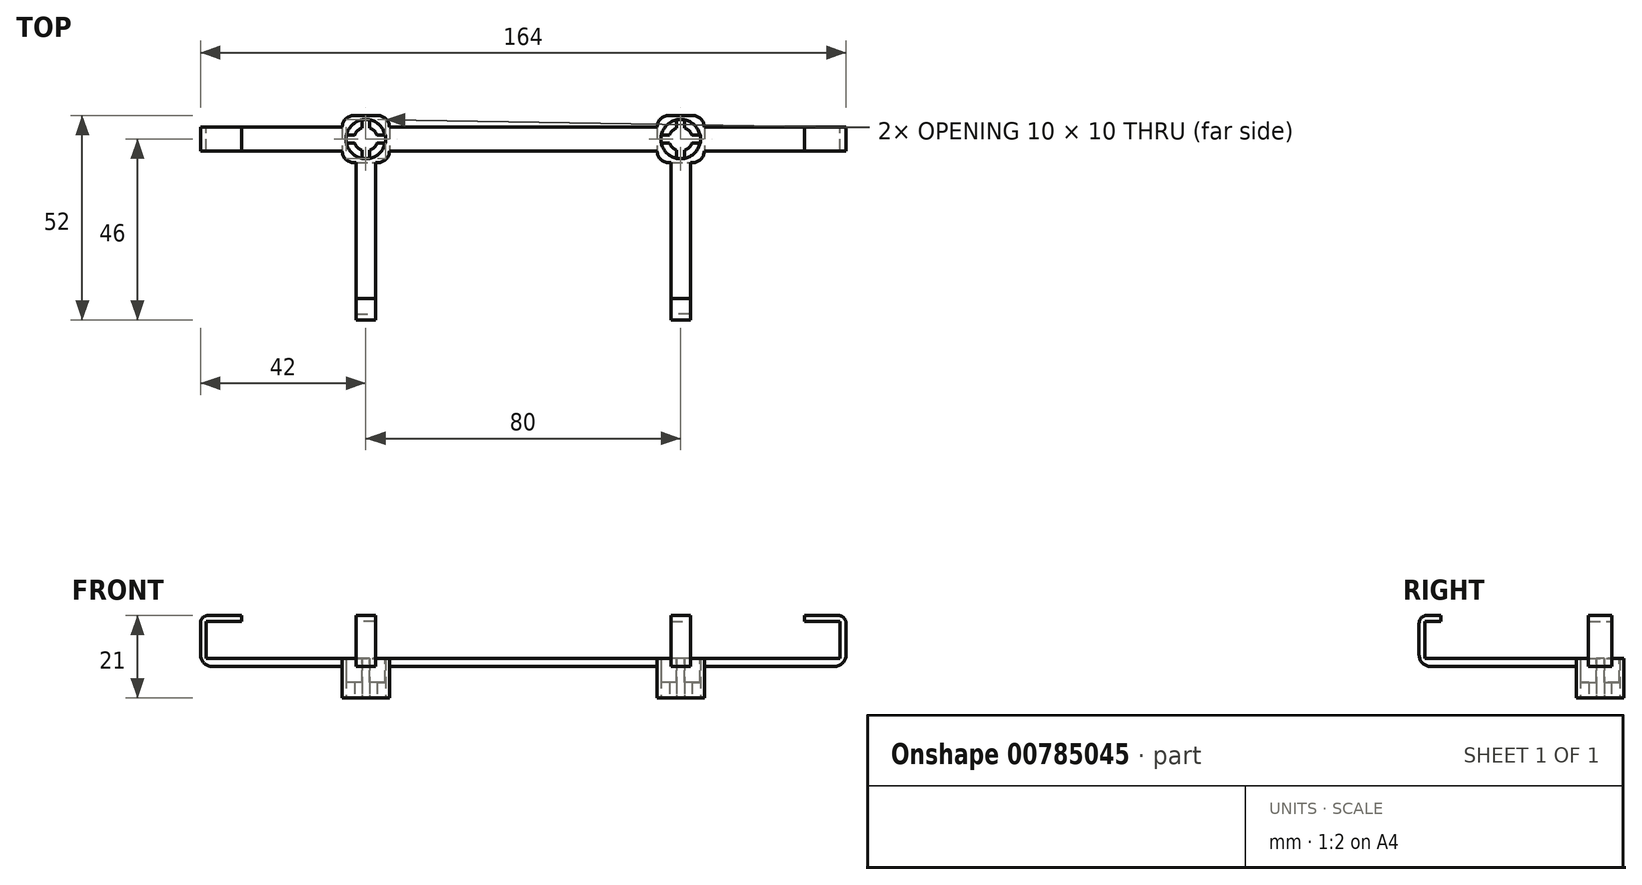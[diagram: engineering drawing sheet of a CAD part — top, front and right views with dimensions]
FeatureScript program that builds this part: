
annotation { "Feature Type Name" : "Feature", "Feature Type Description" : "" }
export const myFeature = defineFeature(function(context is Context, id is Id, definition is map)
    precondition{}
    {
        {
            var Q0;
            Q0=qCreatedBy(makeId("Top.planeOp"),FACE);
            var sketch = newSketch(context, id + "F0", { "sketchPlane" : qUnion([Q0])});
            skLineSegment(sketch, "E0.bottom", {"start": v(82, 3) * mm, "end": v(-82, 3) * mm});
            skLineSegment(sketch, "E0.top", {"start": v(82, -3) * mm, "end": v(-82, -3) * mm});
            skLineSegment(sketch, "E0.left", {"start": v(82, 3) * mm, "end": v(82, -3) * mm});
            skLineSegment(sketch, "E0.right", {"start": v(-82, 3) * mm, "end": v(-82, -3) * mm});
            skPoint(sketch, "E0.middle", {"position": v(0, 0) * mm});
            skLineSegment(sketch, "E1", {"start": v(0, 0) * mm, "end": v(-40, 0) * mm});
            skLineSegment(sketch, "E2", {"start": v(0, 0) * mm, "end": v(40, 0) * mm});
            skLineSegment(sketch, "E3.bottom", {"start": v(-46, 6) * mm, "end": v(-34, 6) * mm});
            skLineSegment(sketch, "E3.top", {"start": v(-46, -6) * mm, "end": v(-34, -6) * mm});
            skLineSegment(sketch, "E3.left", {"start": v(-46, 6) * mm, "end": v(-46, -6) * mm});
            skLineSegment(sketch, "E3.right", {"start": v(-34, 6) * mm, "end": v(-34, -6) * mm});
            skPoint(sketch, "E3.middle", {"position": v(-40, 0) * mm});
            skPoint(sketch, "E4.MirrorP", {"position": v(40, 0) * mm});
            skLineSegment(sketch, "E5.MirrorCS", {"start": v(34, 6) * mm, "end": v(34, -6) * mm});
            skLineSegment(sketch, "E6.MirrorCS", {"start": v(46, 6) * mm, "end": v(46, -6) * mm});
            skLineSegment(sketch, "E7.MirrorCS", {"start": v(46, 6) * mm, "end": v(34, 6) * mm});
            skLineSegment(sketch, "E8.MirrorCS", {"start": v(46, -6) * mm, "end": v(34, -6) * mm});
            skLineSegment(sketch, "E9", {"start": v(-40, -6) * mm, "end": v(-40, -46) * mm});
            skLineSegment(sketch, "E10", {"start": v(-40, -46) * mm, "end": v(-37.5, -46) * mm});
            skLineSegment(sketch, "E11", {"start": v(-37.5, -46) * mm, "end": v(-37.5, -6) * mm});
            skLineSegment(sketch, "E12", {"start": v(-40, -46) * mm, "end": v(-42.5, -46) * mm});
            skLineSegment(sketch, "E13", {"start": v(-42.5, -46) * mm, "end": v(-42.5, -6) * mm});
            skLineSegment(sketch, "E14", {"start": v(0, 0) * mm, "end": v(0, -52.19) * mm});
            skPoint(sketch, "E14.endSnap0", {"position": v(0, -3) * mm});
            skLineSegment(sketch, "E15.MirrorCS", {"start": v(40, -46) * mm, "end": v(42.5, -46) * mm});
            skLineSegment(sketch, "E16.MirrorCS", {"start": v(37.5, -46) * mm, "end": v(37.5, -6) * mm});
            skLineSegment(sketch, "E17.MirrorCS", {"start": v(42.5, -46) * mm, "end": v(42.5, -6) * mm});
            skLineSegment(sketch, "E18.MirrorCS", {"start": v(40, -46) * mm, "end": v(37.5, -46) * mm});
            skLineSegment(sketch, "E19.MirrorCS", {"start": v(40, -6) * mm, "end": v(40, -46) * mm});
            skSolve(sketch);
        }
        {
            var Q0;
            Q0 = qSketchRegion(id + "F0", true);
            extrude(context, id + "F1", {"entities" : qUnion([Q0]), "depth" : 2 * mm, "offsetDistance" : 25 * mm});
        }
        {
            var Q0;
            Q0=makeQuery(id+"F1.opExtrude","CAP_FACE",FACE,{"disambiguationData":[OSD([sQuery(id+"F0.wireOp",EDGE,"E0.bottom"),sQuery(id+"F0.wireOp",EDGE,"E0.top"),sQuery(id+"F0.wireOp",EDGE,"E0.left"),sQuery(id+"F0.wireOp",EDGE,"E0.right"),sQuery(id+"F0.wireOp",EDGE,"E3.bottom"),sQuery(id+"F0.wireOp",EDGE,"E3.top"),sQuery(id+"F0.wireOp",EDGE,"E3.left"),sQuery(id+"F0.wireOp",EDGE,"E3.right"),sQuery(id+"F0.wireOp",EDGE,"E5.MirrorCS"),sQuery(id+"F0.wireOp",EDGE,"E6.MirrorCS"),sQuery(id+"F0.wireOp",EDGE,"E7.MirrorCS"),sQuery(id+"F0.wireOp",EDGE,"E8.MirrorCS"),sQuery(id+"F0.wireOp",EDGE,"E10"),sQuery(id+"F0.wireOp",EDGE,"E11"),sQuery(id+"F0.wireOp",EDGE,"E12"),sQuery(id+"F0.wireOp",EDGE,"E13"),sQuery(id+"F0.wireOp",EDGE,"E15.MirrorCS"),sQuery(id+"F0.wireOp",EDGE,"E16.MirrorCS"),sQuery(id+"F0.wireOp",EDGE,"E17.MirrorCS"),sQuery(id+"F0.wireOp",EDGE,"E18.MirrorCS")])],"isStart":false});
            var sketch = newSketch(context, id + "F2", { "sketchPlane" : qUnion([Q0])});
            skLineSegment(sketch, "E20.bottom", {"start": v(-42.5, -46) * mm, "end": v(-37.5, -46) * mm});
            skLineSegment(sketch, "E20.top", {"start": v(-42.5, -44.5) * mm, "end": v(-37.5, -44.5) * mm});
            skLineSegment(sketch, "E20.left", {"start": v(-42.5, -46) * mm, "end": v(-42.5, -44.5) * mm});
            skLineSegment(sketch, "E20.right", {"start": v(-37.5, -46) * mm, "end": v(-37.5, -44.5) * mm});
            skLineSegment(sketch, "E21.MirrorCS", {"start": v(42.5, -46) * mm, "end": v(42.5, -44.5) * mm});
            skLineSegment(sketch, "E22.MirrorCS", {"start": v(37.5, -46) * mm, "end": v(37.5, -44.5) * mm});
            skLineSegment(sketch, "E23.MirrorCS", {"start": v(42.5, -44.5) * mm, "end": v(37.5, -44.5) * mm});
            skLineSegment(sketch, "E24.MirrorCS", {"start": v(42.5, -46) * mm, "end": v(37.5, -46) * mm});
            skLineSegment(sketch, "E25.bottom", {"start": v(-82, -3) * mm, "end": v(-80.5, -3) * mm});
            skLineSegment(sketch, "E25.top", {"start": v(-82, 3) * mm, "end": v(-80.5, 3) * mm});
            skLineSegment(sketch, "E25.left", {"start": v(-82, -3) * mm, "end": v(-82, 3) * mm});
            skLineSegment(sketch, "E25.right", {"start": v(-80.5, -3) * mm, "end": v(-80.5, 3) * mm});
            skLineSegment(sketch, "E26.MirrorCS", {"start": v(82, -3) * mm, "end": v(80.5, -3) * mm});
            skLineSegment(sketch, "E27.MirrorCS", {"start": v(82, 3) * mm, "end": v(80.5, 3) * mm});
            skLineSegment(sketch, "E28.MirrorCS", {"start": v(80.5, -3) * mm, "end": v(80.5, 3) * mm});
            skLineSegment(sketch, "E29.MirrorCS", {"start": v(82, -3) * mm, "end": v(82, 3) * mm});
            skSolve(sketch);
        }
        {
            var Q0;
            Q0 = qSketchRegion(id + "F2", true);
            extrude(context, id + "F3", {"entities" : qUnion([Q0]), "operationType" : NewBodyOperationType.ADD, "depth" : 11 * mm, "offsetDistance" : 25 * mm});
        }
        {
            var Q0;
            Q0=makeQuery(id+"F3.opExtrude","SWEPT_FACE",FACE,{"disambiguationData":[OSD([sQuery(id+"F2.wireOp",EDGE,"E20.top")])]});
            var sketch = newSketch(context, id + "F4", { "sketchPlane" : qUnion([Q0])});
            skLineSegment(sketch, "E30.bottom", {"start": v(37.5, 13) * mm, "end": v(42.5, 13) * mm});
            skLineSegment(sketch, "E30.top", {"start": v(37.5, 11.5) * mm, "end": v(42.5, 11.5) * mm});
            skLineSegment(sketch, "E30.left", {"start": v(37.5, 13) * mm, "end": v(37.5, 11.5) * mm});
            skLineSegment(sketch, "E30.right", {"start": v(42.5, 13) * mm, "end": v(42.5, 11.5) * mm});
            skLineSegment(sketch, "E31", {"start": v(0, 7.91) * mm, "end": v(0, 17.58) * mm});
            skLineSegment(sketch, "E32.MirrorCS", {"start": v(-37.5, 13) * mm, "end": v(-37.5, 11.5) * mm});
            skLineSegment(sketch, "E33.MirrorCS", {"start": v(-42.5, 13) * mm, "end": v(-42.5, 11.5) * mm});
            skLineSegment(sketch, "E34.MirrorCS", {"start": v(-37.5, 11.5) * mm, "end": v(-42.5, 11.5) * mm});
            skLineSegment(sketch, "E35.MirrorCS", {"start": v(-37.5, 13) * mm, "end": v(-42.5, 13) * mm});
            skSolve(sketch);
        }
        {
            var Q0;
            Q0 = qSketchRegion(id + "F4", true);
            extrude(context, id + "F5", {"entities" : qUnion([Q0]), "operationType" : NewBodyOperationType.ADD, "depth" : 4 * mm, "offsetDistance" : 25 * mm});
        }
        {
            var Q0;
            Q0=makeQuery(id+"F3.opExtrude","SWEPT_FACE",FACE,{"disambiguationData":[OSD([sQuery(id+"F2.wireOp",EDGE,"E28.MirrorCS")])]});
            var sketch = newSketch(context, id + "F6", { "sketchPlane" : qUnion([Q0])});
            skLineSegment(sketch, "E36.bottom", {"start": v(-3, 13) * mm, "end": v(3, 13) * mm});
            skLineSegment(sketch, "E36.top", {"start": v(-3, 11.5) * mm, "end": v(3, 11.5) * mm});
            skLineSegment(sketch, "E36.left", {"start": v(-3, 13) * mm, "end": v(-3, 11.5) * mm});
            skLineSegment(sketch, "E36.right", {"start": v(3, 13) * mm, "end": v(3, 11.5) * mm});
            skSolve(sketch);
        }
        {
            var Q0;
            Q0 = qSketchRegion(id + "F6", true);
            extrude(context, id + "F7", {"entities" : qUnion([Q0]), "operationType" : NewBodyOperationType.ADD, "depth" : 9 * mm, "offsetDistance" : 25 * mm});
        }
        {
            var Q0;
            Q0=makeQuery(id+"F3.opExtrude","SWEPT_FACE",FACE,{"disambiguationData":[OSD([sQuery(id+"F2.wireOp",EDGE,"E25.right")])]});
            var sketch = newSketch(context, id + "F8", { "sketchPlane" : qUnion([Q0])});
            skLineSegment(sketch, "E37.bottom", {"start": v(-3, 13) * mm, "end": v(3, 13) * mm});
            skLineSegment(sketch, "E37.top", {"start": v(-3, 11.5) * mm, "end": v(3, 11.5) * mm});
            skLineSegment(sketch, "E37.left", {"start": v(-3, 13) * mm, "end": v(-3, 11.5) * mm});
            skLineSegment(sketch, "E37.right", {"start": v(3, 13) * mm, "end": v(3, 11.5) * mm});
            skSolve(sketch);
        }
        {
            var Q0;
            Q0 = qSketchRegion(id + "F8", true);
            extrude(context, id + "F9", {"entities" : qUnion([Q0]), "operationType" : NewBodyOperationType.ADD, "depth" : 9 * mm, "offsetDistance" : 25 * mm});
        }
        {
            var Q0;
            Q0=makeQuery(id+"F1.opExtrude","CAP_FACE",FACE,{"disambiguationData":[OSD([sQuery(id+"F0.wireOp",EDGE,"E0.bottom"),sQuery(id+"F0.wireOp",EDGE,"E0.top"),sQuery(id+"F0.wireOp",EDGE,"E0.left"),sQuery(id+"F0.wireOp",EDGE,"E0.right"),sQuery(id+"F0.wireOp",EDGE,"E3.bottom"),sQuery(id+"F0.wireOp",EDGE,"E3.top"),sQuery(id+"F0.wireOp",EDGE,"E3.left"),sQuery(id+"F0.wireOp",EDGE,"E3.right"),sQuery(id+"F0.wireOp",EDGE,"E5.MirrorCS"),sQuery(id+"F0.wireOp",EDGE,"E6.MirrorCS"),sQuery(id+"F0.wireOp",EDGE,"E7.MirrorCS"),sQuery(id+"F0.wireOp",EDGE,"E8.MirrorCS"),sQuery(id+"F0.wireOp",EDGE,"E10"),sQuery(id+"F0.wireOp",EDGE,"E11"),sQuery(id+"F0.wireOp",EDGE,"E12"),sQuery(id+"F0.wireOp",EDGE,"E13"),sQuery(id+"F0.wireOp",EDGE,"E15.MirrorCS"),sQuery(id+"F0.wireOp",EDGE,"E16.MirrorCS"),sQuery(id+"F0.wireOp",EDGE,"E17.MirrorCS"),sQuery(id+"F0.wireOp",EDGE,"E18.MirrorCS")])],"isStart":true});
            var sketch = newSketch(context, id + "F10", { "sketchPlane" : qUnion([Q0])});
            skLineSegment(sketch, "E38.bottom", {"start": v(-46, 6) * mm, "end": v(-34, 6) * mm});
            skLineSegment(sketch, "E38.top", {"start": v(-46, -6) * mm, "end": v(-34, -6) * mm});
            skLineSegment(sketch, "E38.left", {"start": v(-46, 6) * mm, "end": v(-46, -6) * mm});
            skLineSegment(sketch, "E38.right", {"start": v(-34, 6) * mm, "end": v(-34, -6) * mm});
            skLineSegment(sketch, "E39.bottom", {"start": v(34, 6) * mm, "end": v(46, 6) * mm});
            skLineSegment(sketch, "E39.top", {"start": v(34, -6) * mm, "end": v(46, -6) * mm});
            skLineSegment(sketch, "E39.left", {"start": v(34, 6) * mm, "end": v(34, -6) * mm});
            skLineSegment(sketch, "E39.right", {"start": v(46, 6) * mm, "end": v(46, -6) * mm});
            skSolve(sketch);
        }
        {
            var Q0;
            Q0 = qSketchRegion(id + "F10", true);
            extrude(context, id + "F11", {"entities" : qUnion([Q0]), "operationType" : NewBodyOperationType.ADD, "depth" : 8 * mm, "offsetDistance" : 25 * mm});
        }
        {
            var Q0;
            Q0=makeQuery(id+"F1.opExtrude","CAP_FACE",FACE,{"disambiguationData":[OSD([sQuery(id+"F0.wireOp",EDGE,"E0.bottom"),sQuery(id+"F0.wireOp",EDGE,"E0.top"),sQuery(id+"F0.wireOp",EDGE,"E0.left"),sQuery(id+"F0.wireOp",EDGE,"E0.right"),sQuery(id+"F0.wireOp",EDGE,"E3.bottom"),sQuery(id+"F0.wireOp",EDGE,"E3.top"),sQuery(id+"F0.wireOp",EDGE,"E3.left"),sQuery(id+"F0.wireOp",EDGE,"E3.right"),sQuery(id+"F0.wireOp",EDGE,"E5.MirrorCS"),sQuery(id+"F0.wireOp",EDGE,"E6.MirrorCS"),sQuery(id+"F0.wireOp",EDGE,"E7.MirrorCS"),sQuery(id+"F0.wireOp",EDGE,"E8.MirrorCS"),sQuery(id+"F0.wireOp",EDGE,"E10"),sQuery(id+"F0.wireOp",EDGE,"E11"),sQuery(id+"F0.wireOp",EDGE,"E12"),sQuery(id+"F0.wireOp",EDGE,"E13"),sQuery(id+"F0.wireOp",EDGE,"E15.MirrorCS"),sQuery(id+"F0.wireOp",EDGE,"E16.MirrorCS"),sQuery(id+"F0.wireOp",EDGE,"E17.MirrorCS"),sQuery(id+"F0.wireOp",EDGE,"E18.MirrorCS")])],"isStart":false});
            var sketch = newSketch(context, id + "F12", { "sketchPlane" : qUnion([Q0])});
            skCircle(sketch, "E40", {"center": v(-40, 0) * mm, "radius": 5 * mm});
            skPoint(sketch, "E40.centerSnap0", {"position": v(-40, 6) * mm});
            skLineSegment(sketch, "E41", {"start": v(0, 7.73) * mm, "end": v(0, -9.35) * mm});
            skPoint(sketch, "E41.endSnap0", {"position": v(0, 3) * mm});
            skPoint(sketch, "E42.MirrorP", {"position": v(40, 6) * mm});
            skCircle(sketch, "E43.MirrorC", {"center": v(40, 0) * mm, "radius": 5 * mm});
            skSolve(sketch);
        }
        {
            var Q0;
            Q0 = qSketchRegion(id + "F12", true);
            extrude(context, id + "F13", {"entities" : qUnion([Q0]), "operationType" : NewBodyOperationType.REMOVE, "oppositeDirection" : true, "depth" : 6 * mm, "offsetDistance" : 25 * mm});
        }
        {
            var Q0;
            Q0=makeQuery(id+"F11.opExtrude","CAP_FACE",FACE,{"disambiguationData":[OSD([sQuery(id+"F10.wireOp",EDGE,"E39.bottom"),sQuery(id+"F10.wireOp",EDGE,"E39.top"),sQuery(id+"F10.wireOp",EDGE,"E39.left"),sQuery(id+"F10.wireOp",EDGE,"E39.right")])],"isStart":false});
            var sketch = newSketch(context, id + "F14", { "sketchPlane" : qUnion([Q0])});
            skCircle(sketch, "E44", {"center": v(40, 0) * mm, "radius": 3 * mm});
            skPoint(sketch, "E44.centerSnap0", {"position": v(40, 6) * mm});
            skPoint(sketch, "E45.MirrorP", {"position": v(-40, 6) * mm});
            skCircle(sketch, "E46.MirrorC", {"center": v(-40, 0) * mm, "radius": 3 * mm});
            skLineSegment(sketch, "E47", {"start": v(-40, 5) * mm, "end": v(-39, 5) * mm});
            skLineSegment(sketch, "E48", {"start": v(-39, 5) * mm, "end": v(-39, 2.83) * mm});
            skLineSegment(sketch, "E49.MirrorCS", {"start": v(-40, 5) * mm, "end": v(-41, 5) * mm});
            skLineSegment(sketch, "E50.MirrorCS", {"start": v(-41, 5) * mm, "end": v(-41, 2.83) * mm});
            skLineSegment(sketch, "E51.MirrorCS", {"start": v(-39, -5) * mm, "end": v(-39, -2.83) * mm});
            skLineSegment(sketch, "E52.MirrorCS", {"start": v(-40, -5) * mm, "end": v(-39, -5) * mm});
            skLineSegment(sketch, "E53.MirrorCS", {"start": v(-41, -5) * mm, "end": v(-41, -2.83) * mm});
            skLineSegment(sketch, "E54.MirrorCS", {"start": v(-40, -5) * mm, "end": v(-41, -5) * mm});
            skLineSegment(sketch, "E55", {"start": v(-35, 0) * mm, "end": v(-35, -1) * mm});
            skLineSegment(sketch, "E56", {"start": v(-35, -1) * mm, "end": v(-37.17, -1) * mm});
            skLineSegment(sketch, "E57.MirrorCS", {"start": v(-35, 1) * mm, "end": v(-37.17, 1) * mm});
            skLineSegment(sketch, "E58.MirrorCS", {"start": v(-35, 0) * mm, "end": v(-35, 1) * mm});
            skLineSegment(sketch, "E59.MirrorCS", {"start": v(-45, 1) * mm, "end": v(-42.83, 1) * mm});
            skLineSegment(sketch, "E60.MirrorCS", {"start": v(-45, 0) * mm, "end": v(-45, 1) * mm});
            skLineSegment(sketch, "E61.MirrorCS", {"start": v(-45, -1) * mm, "end": v(-42.83, -1) * mm});
            skLineSegment(sketch, "E62.MirrorCS", {"start": v(-45, 0) * mm, "end": v(-45, -1) * mm});
            skLineSegment(sketch, "E63.MirrorCS", {"start": v(35, 0) * mm, "end": v(35, -1) * mm});
            skLineSegment(sketch, "E64.MirrorCS", {"start": v(35, 0) * mm, "end": v(35, 1) * mm});
            skLineSegment(sketch, "E65.MirrorCS", {"start": v(45, 0) * mm, "end": v(45, -1) * mm});
            skLineSegment(sketch, "E66.MirrorCS", {"start": v(40, 5) * mm, "end": v(41, 5) * mm});
            skLineSegment(sketch, "E67.MirrorCS", {"start": v(40, 5) * mm, "end": v(39, 5) * mm});
            skLineSegment(sketch, "E68.MirrorCS", {"start": v(45, 0) * mm, "end": v(45, 1) * mm});
            skLineSegment(sketch, "E69.MirrorCS", {"start": v(40, -5) * mm, "end": v(39, -5) * mm});
            skLineSegment(sketch, "E70.MirrorCS", {"start": v(40, -5) * mm, "end": v(41, -5) * mm});
            skLineSegment(sketch, "E71.MirrorCS", {"start": v(45, -1) * mm, "end": v(42.83, -1) * mm});
            skLineSegment(sketch, "E72.MirrorCS", {"start": v(35, 1) * mm, "end": v(37.17, 1) * mm});
            skLineSegment(sketch, "E73.MirrorCS", {"start": v(35, -1) * mm, "end": v(37.17, -1) * mm});
            skLineSegment(sketch, "E74.MirrorCS", {"start": v(39, 5) * mm, "end": v(39, 2.83) * mm});
            skLineSegment(sketch, "E75.MirrorCS", {"start": v(39, -5) * mm, "end": v(39, -2.83) * mm});
            skLineSegment(sketch, "E76.MirrorCS", {"start": v(41, 5) * mm, "end": v(41, 2.83) * mm});
            skLineSegment(sketch, "E77.MirrorCS", {"start": v(45, 1) * mm, "end": v(42.83, 1) * mm});
            skLineSegment(sketch, "E78.MirrorCS", {"start": v(41, -5) * mm, "end": v(41, -2.83) * mm});
            skSolve(sketch);
        }
        {
            var Q0;
            Q0 = qSketchRegion(id + "F14", true);
            extrude(context, id + "F15", {"entities" : qUnion([Q0]), "operationType" : NewBodyOperationType.REMOVE, "oppositeDirection" : true, "depth" : 10 * mm, "offsetDistance" : 25 * mm});
        }
        {
            var Q0;
            Q0=makeQuery(id+"F11.boolean.opBoolean","MERGE",EDGE,{"derivedFrom":[makeQuery(id+"F1.opExtrude","SWEPT_EDGE",EDGE,{"disambiguationData":[OSD([sQuery(id+"F0.wireOp",EDGE,"E3.bottom"),sQuery(id+"F0.wireOp",EDGE,"E3.left")])]}),makeQuery(id+"F11.opExtrude","SWEPT_EDGE",EDGE,{"disambiguationData":[OSD([sQuery(id+"F10.wireOp",EDGE,"E38.top"),sQuery(id+"F10.wireOp",EDGE,"E38.left")])]})]});
            var Q1;
            Q1=makeQuery(id+"F11.boolean.opBoolean","MERGE",EDGE,{"derivedFrom":[makeQuery(id+"F1.opExtrude","SWEPT_EDGE",EDGE,{"disambiguationData":[OSD([sQuery(id+"F0.wireOp",EDGE,"E3.bottom"),sQuery(id+"F0.wireOp",EDGE,"E3.right")])]}),makeQuery(id+"F11.opExtrude","SWEPT_EDGE",EDGE,{"disambiguationData":[OSD([sQuery(id+"F10.wireOp",EDGE,"E38.top"),sQuery(id+"F10.wireOp",EDGE,"E38.right")])]})]});
            var Q2;
            Q2=makeQuery(id+"F11.boolean.opBoolean","MERGE",EDGE,{"derivedFrom":[makeQuery(id+"F1.opExtrude","SWEPT_EDGE",EDGE,{"disambiguationData":[OSD([sQuery(id+"F0.wireOp",EDGE,"E3.top"),sQuery(id+"F0.wireOp",EDGE,"E3.right")])]}),makeQuery(id+"F11.opExtrude","SWEPT_EDGE",EDGE,{"disambiguationData":[OSD([sQuery(id+"F10.wireOp",EDGE,"E38.bottom"),sQuery(id+"F10.wireOp",EDGE,"E38.right")])]})]});
            var Q3;
            Q3=makeQuery(id+"F11.boolean.opBoolean","MERGE",EDGE,{"derivedFrom":[makeQuery(id+"F1.opExtrude","SWEPT_EDGE",EDGE,{"disambiguationData":[OSD([sQuery(id+"F0.wireOp",EDGE,"E3.top"),sQuery(id+"F0.wireOp",EDGE,"E3.left")])]}),makeQuery(id+"F11.opExtrude","SWEPT_EDGE",EDGE,{"disambiguationData":[OSD([sQuery(id+"F10.wireOp",EDGE,"E38.bottom"),sQuery(id+"F10.wireOp",EDGE,"E38.left")])]})]});
            var Q4;
            Q4=makeQuery(id+"F11.boolean.opBoolean","MERGE",EDGE,{"derivedFrom":[makeQuery(id+"F1.opExtrude","SWEPT_EDGE",EDGE,{"disambiguationData":[OSD([sQuery(id+"F0.wireOp",EDGE,"E6.MirrorCS"),sQuery(id+"F0.wireOp",EDGE,"E7.MirrorCS")])]}),makeQuery(id+"F11.opExtrude","SWEPT_EDGE",EDGE,{"disambiguationData":[OSD([sQuery(id+"F10.wireOp",EDGE,"E39.top"),sQuery(id+"F10.wireOp",EDGE,"E39.right")])]})]});
            var Q5;
            Q5=makeQuery(id+"F11.boolean.opBoolean","MERGE",EDGE,{"derivedFrom":[makeQuery(id+"F1.opExtrude","SWEPT_EDGE",EDGE,{"disambiguationData":[OSD([sQuery(id+"F0.wireOp",EDGE,"E5.MirrorCS"),sQuery(id+"F0.wireOp",EDGE,"E7.MirrorCS")])]}),makeQuery(id+"F11.opExtrude","SWEPT_EDGE",EDGE,{"disambiguationData":[OSD([sQuery(id+"F10.wireOp",EDGE,"E39.top"),sQuery(id+"F10.wireOp",EDGE,"E39.left")])]})]});
            var Q6;
            Q6=makeQuery(id+"F11.boolean.opBoolean","MERGE",EDGE,{"derivedFrom":[makeQuery(id+"F1.opExtrude","SWEPT_EDGE",EDGE,{"disambiguationData":[OSD([sQuery(id+"F0.wireOp",EDGE,"E6.MirrorCS"),sQuery(id+"F0.wireOp",EDGE,"E8.MirrorCS")])]}),makeQuery(id+"F11.opExtrude","SWEPT_EDGE",EDGE,{"disambiguationData":[OSD([sQuery(id+"F10.wireOp",EDGE,"E39.bottom"),sQuery(id+"F10.wireOp",EDGE,"E39.right")])]})]});
            var Q7;
            Q7=makeQuery(id+"F11.boolean.opBoolean","MERGE",EDGE,{"derivedFrom":[makeQuery(id+"F1.opExtrude","SWEPT_EDGE",EDGE,{"disambiguationData":[OSD([sQuery(id+"F0.wireOp",EDGE,"E5.MirrorCS"),sQuery(id+"F0.wireOp",EDGE,"E8.MirrorCS")])]}),makeQuery(id+"F11.opExtrude","SWEPT_EDGE",EDGE,{"disambiguationData":[OSD([sQuery(id+"F10.wireOp",EDGE,"E39.bottom"),sQuery(id+"F10.wireOp",EDGE,"E39.left")])]})]});
            var Q8;
            Q8=makeQuery(id+"F1.opExtrude","CAP_EDGE",EDGE,{"disambiguationData":[OSD([sQuery(id+"F0.wireOp",EDGE,"E15.MirrorCS"),sQuery(id+"F0.wireOp",EDGE,"E18.MirrorCS")])],"isStart":true});
            var Q9;
            Q9=makeQuery(id+"F1.opExtrude","CAP_EDGE",EDGE,{"disambiguationData":[OSD([sQuery(id+"F0.wireOp",EDGE,"E10"),sQuery(id+"F0.wireOp",EDGE,"E12")])],"isStart":true});
            var Q10;
            Q10=makeQuery(id+"F1.opExtrude","CAP_EDGE",EDGE,{"disambiguationData":[OSD([sQuery(id+"F0.wireOp",EDGE,"E0.right")])],"isStart":true});
            var Q11;
            Q11=makeQuery(id+"F1.opExtrude","CAP_EDGE",EDGE,{"disambiguationData":[OSD([sQuery(id+"F0.wireOp",EDGE,"E0.left")])],"isStart":true});
            fillet(context, id + "F16", {"entities" : qUnion([Q0, Q1, Q2, Q3, Q4, Q5, Q6, Q7, Q8, Q9, Q10, Q11]), "radius" : 3 * mm, "tangentPropagation" : true, "allowEdgeOverflow" : false});
        }
        {
            var Q0;
            Q0=makeQuery(id+"F3.opExtrude","CAP_EDGE",EDGE,{"disambiguationData":[OSD([sQuery(id+"F2.wireOp",EDGE,"E25.left")])],"isStart":false});
            var Q1;
            Q1=makeQuery(id+"F3.opExtrude","CAP_EDGE",EDGE,{"disambiguationData":[OSD([sQuery(id+"F2.wireOp",EDGE,"E20.bottom")])],"isStart":false});
            var Q2;
            Q2=makeQuery(id+"F3.opExtrude","CAP_EDGE",EDGE,{"disambiguationData":[OSD([sQuery(id+"F2.wireOp",EDGE,"E24.MirrorCS")])],"isStart":false});
            var Q3;
            Q3=makeQuery(id+"F3.opExtrude","CAP_EDGE",EDGE,{"disambiguationData":[OSD([sQuery(id+"F2.wireOp",EDGE,"E29.MirrorCS")])],"isStart":false});
            fillet(context, id + "F17", {"entities" : qUnion([Q0, Q1, Q2, Q3]), "radius" : 2 * mm, "tangentPropagation" : true, "allowEdgeOverflow" : false});
        }
    });
